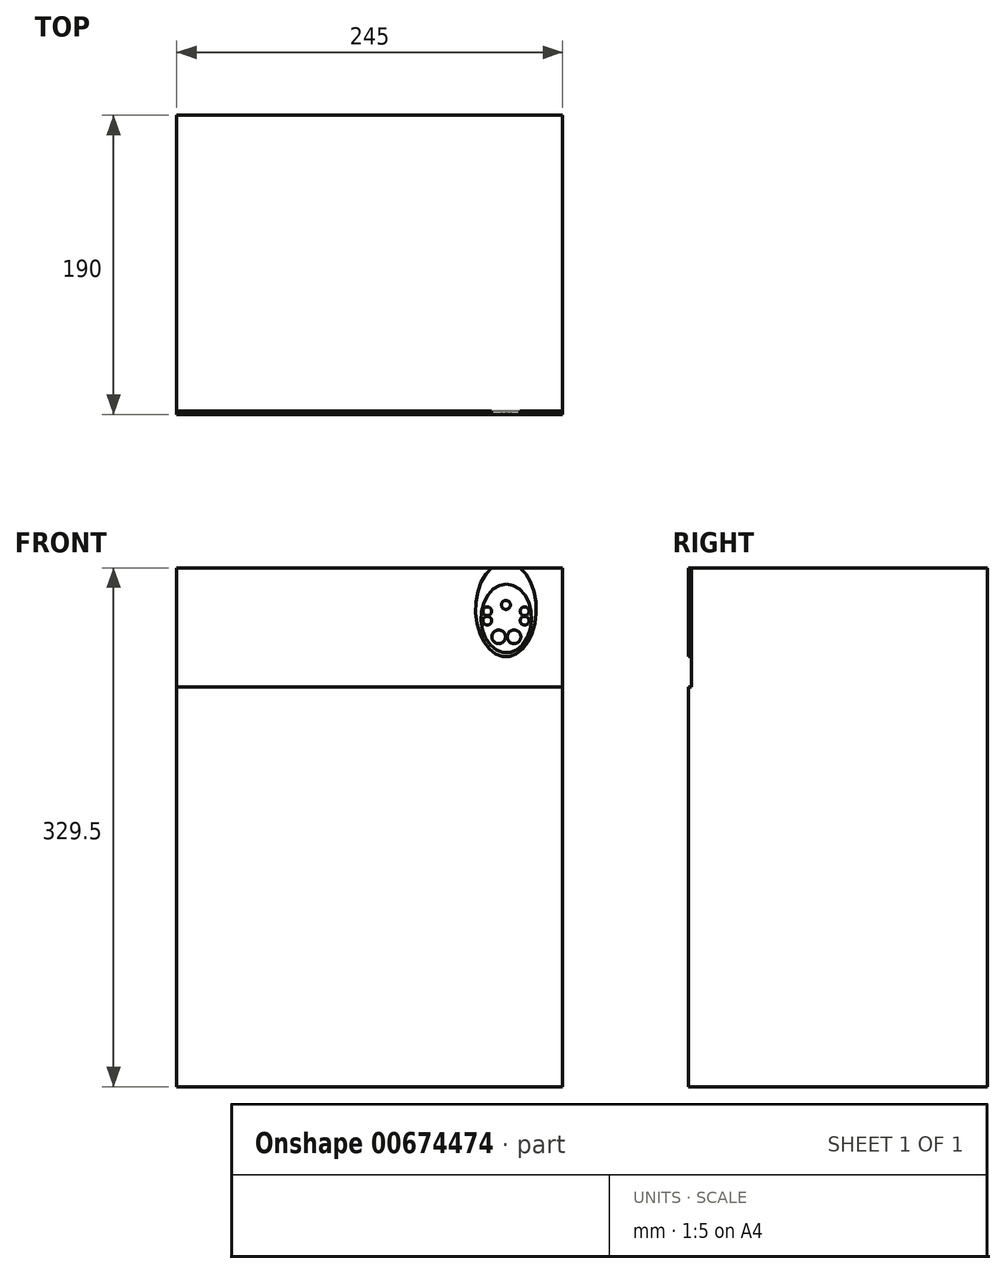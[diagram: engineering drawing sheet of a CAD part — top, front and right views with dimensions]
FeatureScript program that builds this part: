
annotation { "Feature Type Name" : "Feature", "Feature Type Description" : "" }
export const myFeature = defineFeature(function(context is Context, id is Id, definition is map)
    precondition{}
    {
        {
            var Q0;
            Q0=qCreatedBy(makeId("Front.planeOp"),FACE);
            var sketch = newSketch(context, id + "F0", { "sketchPlane" : qUnion([Q0])});
            skLineSegment(sketch, "E0.bottom", {"start": v(122.5, 164.75) * mm, "end": v(-122.5, 164.75) * mm});
            skLineSegment(sketch, "E0.top", {"start": v(122.5, -164.75) * mm, "end": v(-122.5, -164.75) * mm});
            skLineSegment(sketch, "E0.left", {"start": v(122.5, 164.75) * mm, "end": v(122.5, -164.75) * mm});
            skLineSegment(sketch, "E0.right", {"start": v(-122.5, 164.75) * mm, "end": v(-122.5, -164.75) * mm});
            skPoint(sketch, "E0.middle", {"position": v(0, 0) * mm});
            skSolve(sketch);
        }
        {
            var Q0;
            Q0=makeQuery(id+"F0.imprint","IMPRINT",FACE,{"disambiguationData":[TD([[makeQuery(id+"F0.imprint","IMPRINT",EDGE,{"derivedFrom":sQuery(id+"F0.wireOp",EDGE,"E0.bottom")}),1.0]])]});
            extrude(context, id + "F1", {"entities" : qUnion([Q0]), "depth" : 190 * mm, "offsetDistance" : 25 * mm});
        }
        {
            var Q0;
            Q0=makeQuery(id+"F1.opExtrude","CAP_FACE",FACE,{"disambiguationData":[OSD([sQuery(id+"F0.wireOp",EDGE,"E0.bottom"),sQuery(id+"F0.wireOp",EDGE,"E0.top"),sQuery(id+"F0.wireOp",EDGE,"E0.left"),sQuery(id+"F0.wireOp",EDGE,"E0.right")])],"isStart":false});
            var sketch = newSketch(context, id + "F2", { "sketchPlane" : qUnion([Q0])});
            skEllipse(sketch, "E1", {"center": v(86.89, 132.7) * mm, "majorRadius": 21.83 * mm, "minorRadius": 16.04 * mm, "majorAxis": v(0, 1)});
            skEllipse(sketch, "E2", {"center": v(86.61, 138.36) * mm, "majorRadius": 29.93 * mm, "minorRadius": 19.27 * mm, "majorAxis": v(0, 1)});
            skCircle(sketch, "E3", {"center": v(82, 120.97) * mm, "radius": 4.32 * mm});
            skCircle(sketch, "E4.MirrorC", {"center": v(91.77, 120.97) * mm, "radius": 4.32 * mm});
            skCircle(sketch, "E5", {"center": v(74.76, 131.23) * mm, "radius": 2.8 * mm});
            skCircle(sketch, "E6.MirrorC", {"center": v(74.76, 137.22) * mm, "radius": 2.8 * mm});
            skCircle(sketch, "E7.MirrorC", {"center": v(98.46, 131.23) * mm, "radius": 2.8 * mm});
            skCircle(sketch, "E8.MirrorC", {"center": v(98.46, 137.22) * mm, "radius": 2.8 * mm});
            skCircle(sketch, "E9", {"center": v(86.61, 141.26) * mm, "radius": 2.85 * mm});
            skLineSegment(sketch, "E10", {"start": v(-122.5, 89.19) * mm, "end": v(122.5, 89.19) * mm});
            skSolve(sketch);
        }
        {
            var Q0;
            Q0=makeQuery(id+"F2.imprint","IMPRINT",FACE,{"disambiguationData":[TD([[makeQuery(id+"F2.imprint","IMPRINT",EDGE,{"derivedFrom":sQuery(id+"F2.wireOp",EDGE,"E1")}),1.0]])]});
            var Q1;
            Q1=makeQuery(id+"F2.imprint","IMPRINT",FACE,{"disambiguationData":[TD([[makeQuery(id+"F2.imprint","IMPRINT",EDGE,{"derivedFrom":sQuery(id+"F2.wireOp",EDGE,"aSmwqvFC-2Ay4-zH53-tjZq-JXV0DR2VfAVj.top")}),1.0]])]});
            var Q2;
            {var subQ8=sQuery(id+"F2.wireOp",EDGE,"E10");Q2=makeQuery(id+"F2.imprint","IMPRINT",FACE,{"disambiguationData":[TD([[makeQuery(id+"F2.imprint","IMPRINT",EDGE,{"derivedFrom":subQ8}),1.0]])]});}
            extrude(context, id + "F3", {"entities" : qUnion([Q0, Q1, Q2]), "operationType" : NewBodyOperationType.REMOVE, "oppositeDirection" : true, "depth" : 2 * mm, "offsetDistance" : 25 * mm});
        }
    });
